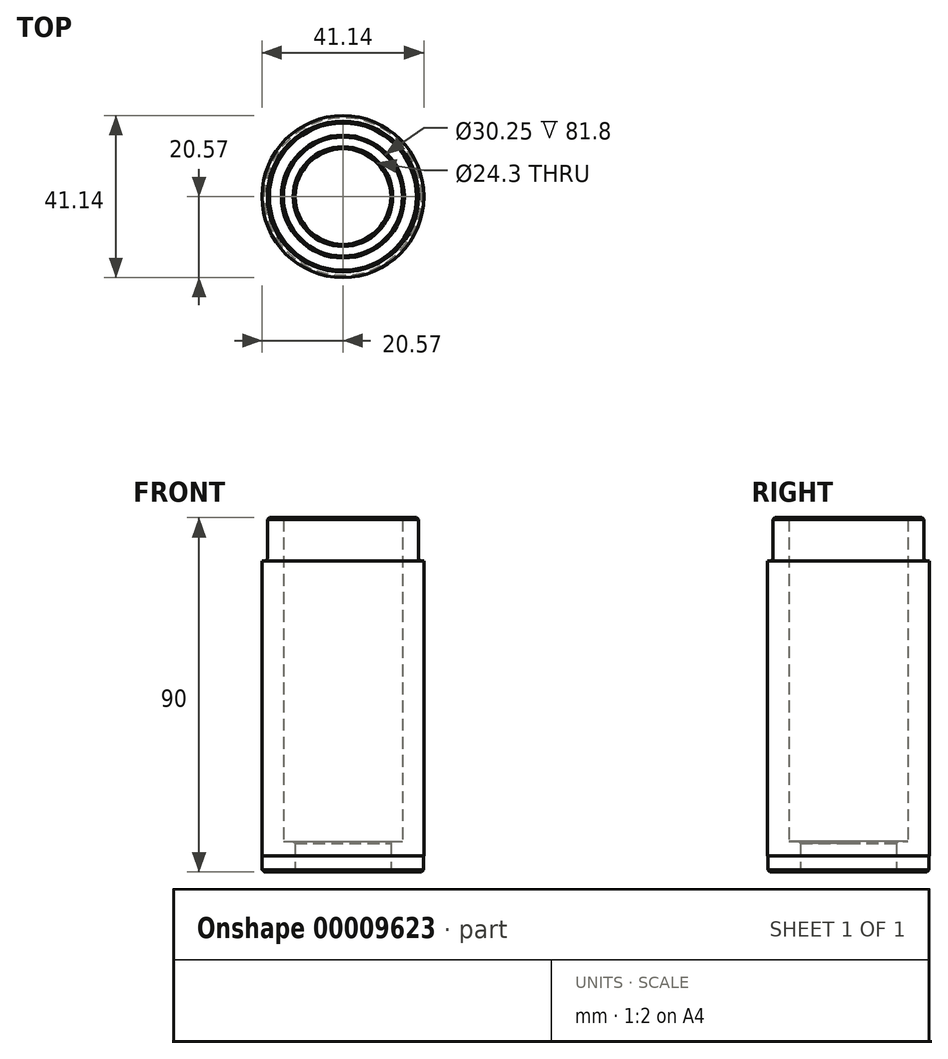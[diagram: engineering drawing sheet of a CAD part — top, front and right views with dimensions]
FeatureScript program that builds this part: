
annotation { "Feature Type Name" : "Feature", "Feature Type Description" : "" }
export const myFeature = defineFeature(function(context is Context, id is Id, definition is map)
    precondition{}
    {
        {
            var Q0;
            Q0=qCreatedBy(makeId("Front.planeOp"),FACE);
            var sketch = newSketch(context, id + "F0", { "sketchPlane" : qUnion([Q0])});
            skLineSegment(sketch, "E0.rect.bottom", {"start": v(19.2, 45) * mm, "end": v(-19.2, 45) * mm});
            skLineSegment(sketch, "E0.rect.top", {"start": v(19.43, -45) * mm, "end": v(-20.5, -45) * mm});
            skLineSegment(sketch, "E0.rect.left", {"start": v(19.43, 34) * mm, "end": v(19.43, -45) * mm});
            skLineSegment(sketch, "E0.rect.right", {"start": v(-20.57, 34) * mm, "end": v(-20.57, -41) * mm});
            skPoint(sketch, "E0.rect.middle", {"position": v(0, 0) * mm});
            skLineSegment(sketch, "E1.rect.bottom", {"start": v(15.12, 45) * mm, "end": v(-15.12, 45) * mm});
            skLineSegment(sketch, "E1.rect.top", {"start": v(15.12, -45) * mm, "end": v(-15.12, -45) * mm});
            skLineSegment(sketch, "E1.rect.left", {"start": v(15.12, 45) * mm, "end": v(15.12, -37.3) * mm});
            skLineSegment(sketch, "E1.rect.right", {"start": v(-15.12, 45) * mm, "end": v(-15.12, -37.3) * mm});
            skLineSegment(sketch, "E2.rect.left", {"start": v(12.15, -37.3) * mm, "end": v(12.15, -45) * mm});
            skLineSegment(sketch, "E2.rect.right", {"start": v(-12.15, -37.3) * mm, "end": v(-12.15, -45) * mm});
            skPoint(sketch, "E2.rect.middle", {"position": v(-0.57, -45) * mm});
            skLineSegment(sketch, "E3", {"start": v(-12.15, -37.3) * mm, "end": v(-15.12, -37.3) * mm});
            skLineSegment(sketch, "E4", {"start": v(12.15, -37.3) * mm, "end": v(15.12, -37.3) * mm});
            skLineSegment(sketch, "E5.rect.left", {"start": v(19.2, 45) * mm, "end": v(19.2, 34) * mm});
            skLineSegment(sketch, "E5.rect.right", {"start": v(-19.2, 45) * mm, "end": v(-19.2, 34) * mm});
            skPoint(sketch, "E5.rect.middle", {"position": v(0, 26.77) * mm});
            skPoint(sketch, "E6.orphan", {"position": v(-19.2, 39.16) * mm});
            skPoint(sketch, "E7.orphan", {"position": v(19.2, 39.16) * mm});
            skPoint(sketch, "E8.orphan", {"position": v(-19.2, 14.37) * mm});
            skPoint(sketch, "E9.orphan", {"position": v(19.2, 14.37) * mm});
            skLineSegment(sketch, "E10", {"start": v(-19.2, 34) * mm, "end": v(17.4, 34) * mm});
            skLineSegment(sketch, "E11", {"start": v(17.4, 34) * mm, "end": v(19.2, 34) * mm});
            skLineSegment(sketch, "E12", {"start": v(19.2, 34) * mm, "end": v(19.2, 34) * mm});
            skLineSegment(sketch, "E13", {"start": v(-19.2, 34) * mm, "end": v(-20.57, 34) * mm});
            skLineSegment(sketch, "E14", {"start": v(19.2, 34) * mm, "end": v(19.43, 34) * mm});
            skLineSegment(sketch, "E15", {"start": v(0, -67.17) * mm, "end": v(0, 69.5) * mm});
            skPoint(sketch, "E15.endSnap0", {"position": v(0, 45) * mm});
            skLineSegment(sketch, "E16", {"start": v(-20.5, -45) * mm, "end": v(-20.5, -41) * mm});
            skLineSegment(sketch, "E17", {"start": v(-20.5, -41) * mm, "end": v(-20.57, -41) * mm});
            skLineSegment(sketch, "E18", {"start": v(19.36, -45) * mm, "end": v(19.36, -41) * mm});
            skLineSegment(sketch, "E19", {"start": v(19.36, -41) * mm, "end": v(19.43, -41) * mm});
            skSolve(sketch);
        }
        {
            var Q0;
            {var subQ3=sQuery(id+"F0.wireOp",EDGE,"E5.rect.right");Q0=makeQuery(id+"F0.imprint","IMPRINT",FACE,{"disambiguationData":[TD([[makeQuery(id+"F0.imprint","IMPRINT",EDGE,{"derivedFrom":subQ3}),1.0]])]});}
            var Q1;
            {var subQ9=sQuery(id+"F0.wireOp",EDGE,"E0.rect.right");Q1=makeQuery(id+"F0.imprint","IMPRINT",FACE,{"disambiguationData":[TD([[makeQuery(id+"F0.imprint","IMPRINT",EDGE,{"derivedFrom":subQ9}),1.0]])]});}
            var Q2;
            Q2=sQuery(id+"F0.wireOp",EDGE,"E15");
            revolve(context, id + "F1", {"entities" : qUnion([Q0, Q1]), "axis" : qUnion([Q2]), "revolveType" : RevolveType.FULL});
        }
        {
            var Q0;
            Q0=makeQuery(id+"F1.opRevolve","SWEPT_EDGE",EDGE,{"disambiguationData":[OSD([sQuery(id+"F0.wireOp",EDGE,"E5.rect.right"),sQuery(id+"F0.wireOp",EDGE,"E10"),sQuery(id+"F0.wireOp",EDGE,"E13")])]});
            fillet(context, id + "F2", {"entities" : qUnion([Q0]), "radius" : .75 * mm, "tangentPropagation" : true, "allowEdgeOverflow" : false});
        }
        {
            var Q0;
            Q0=makeQuery(id+"F1.opRevolve","SWEPT_EDGE",EDGE,{"disambiguationData":[OSD([sQuery(id+"F0.wireOp",EDGE,"E0.rect.bottom"),sQuery(id+"F0.wireOp",EDGE,"E5.rect.right")])]});
            var Q1;
            Q1=makeQuery(id+"F1.opRevolve","SWEPT_EDGE",EDGE,{"disambiguationData":[OSD([sQuery(id+"F0.wireOp",EDGE,"E0.rect.bottom"),sQuery(id+"F0.wireOp",EDGE,"E1.rect.bottom"),sQuery(id+"F0.wireOp",EDGE,"E1.rect.right")])]});
            var Q2;
            Q2=makeQuery(id+"F1.opRevolve","SWEPT_EDGE",EDGE,{"disambiguationData":[OSD([sQuery(id+"F0.wireOp",EDGE,"E0.rect.top"),sQuery(id+"F0.wireOp",EDGE,"E16")])]});
            var Q3;
            Q3=makeQuery(id+"F1.opRevolve","SWEPT_EDGE",EDGE,{"disambiguationData":[OSD([sQuery(id+"F0.wireOp",EDGE,"E1.rect.top"),sQuery(id+"F0.wireOp",EDGE,"E2.rect.right")])]});
            chamfer(context, id + "F3", {"entities" : qUnion([Q0, Q1, Q2, Q3]), "width" : .5 * mm, "tangentPropagation" : true});
        }
    });
